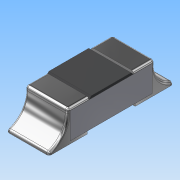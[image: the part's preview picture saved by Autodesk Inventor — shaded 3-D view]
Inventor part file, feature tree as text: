
AUTODESK INVENTOR PART (.ipt)
format: ipt  version: 2016 (Build 200138000, 138)  size: 205,824 bytes
history: native  units: mm
features: extrude x2, fillet x2, sketch x1, mirror x1
ambient origin geometry x8: Origin, YZ Plane, XZ Plane, XY Plane, X Axis, Y Axis, Z Axis, Center Point
bodies: Body1 (feature_tree)
feature tree (6):
  sketch  "Sketch10"  dims[d9=0.499mm d10=0.0mm d11=0.2mm d12=0.45mm d13=0.03mm d14=0.03mm d15=0.25mm d16=45.0deg d17=0.5mm d18=0.0mm d19=0.03mm d21=1.0mm d22=0.37mm d23=0.3mm d24=0.029mm]
  extrude  "Extrusion4"  Depth=0.2mm
  extrude  "Extrusion5"  Depth=0.45mm
  fillet  "Fillet2"  Radius=0.03mm
  fillet  "Fillet3"  Radius=0.03mm
  mirror  "Mirror1"
